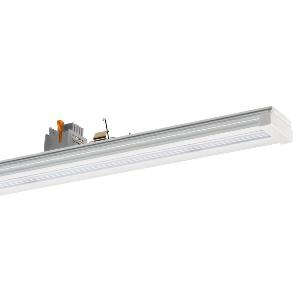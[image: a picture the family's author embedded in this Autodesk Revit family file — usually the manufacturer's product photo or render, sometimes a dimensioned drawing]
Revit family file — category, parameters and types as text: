
# Revit family: conveo_-_cvg_4500_840_w-p_da_7_226848019-00804937_9bd9
name_source: partatom
category: Lighting Fixtures
units: mm (PartAtom-declared; Revit-internal decimal feet)

## family parameters
Cut with Voids When Loaded = No
Host = Face
Light Source = No
Part Type = Normal
Room Calculation Point = No
Round Connector Dimension = Use Diameter
Shared = No

## types (1)
- CONVEO - CVG 4500/840/W-P/DA/7 (1 x LED, 4400 lm, 4000K)
    Apparent Load = 28 VA
    Approval mark = CE
    CIE Flux Codes = 54 85 97 100 100
    Color Rendering = 80-89
    Color Temperature = 4000K
    Control Gear = Electronic ballast
    Default Elevation = 1800 mm
    Description = CVG 4500/840/W-P/DA/7|Continuous-row system|light source: LED|work equipment: Adjustable electronic ballast, digital DALI|connected load: 220-240 V, 50-60 Hz|Power consumption: approx. 28 W|luminous flux: 4400 lm|luminous efficacy: 157 lm/W|colour temperature: Cold white, ca. 4000 K|color rendering index (CRI): >= 80|chromaticity tolerance:  3 SDCM|System of protection: IP 54|class of protection: I|technology: Continuously dimmable|luminaire body|material: Aluminium|surface: Powder coatet|colour: White|lamp cover: Acrylic (PMMA), Satine|weight (net): approx. 1.9 kg|Fastening: Available separately|minimum ambient temperature: -25 ░C|maximum ambient temperature: 55 ░C|glare control: Prism optics (linear)|Approval mark: VDE - ENEC|
    Frequency = 50 Hz
    Height = 70 mm
    Lamp = 1 x LED
    Lamp Light Flux = 4400 lm
    Lamp count = 1
    Length = 1500 mm
    Luminous efficacy = 157 lm/W
    Manufacturer = Waldmann
    ModVariant = No
    Model = 226848019-00804937
    Mounting Place = Ceiling
    Mounting Type = Pendant
    Number of Poles = 1
    OnlyDefault = Yes
    Power Factor = 1
    Product Name = CONVEO - CVG 4500/840/W-P/DA/7
    Product group = Continuous-row system (industry)
    ProductGroupID = 301
    Protection Class = Protection class I
    Protection Degree = IP 54
    RLX_Detail_Level = 1
    RlxData = <blob elided: 99077 chars, md5=085253d9>
    Socket = socket
    Standby Power = 0 W
    System Light Flux = 4400 lm
    System Power = 28 W
    Type Comments = Product without accessories
    Type Image = 226848019-00804937-1p7.jpg
    URL = http://relux.com
    VarID = ---
    Voltage = 230 V
    Voltage Range = 220-240 V
    Weight = 0.00 kg
    Width = 64 mm

## geometry (parser evidence)
native form markers: Blend x4, Sweep x10
no freeform markers — native parametric forms only
